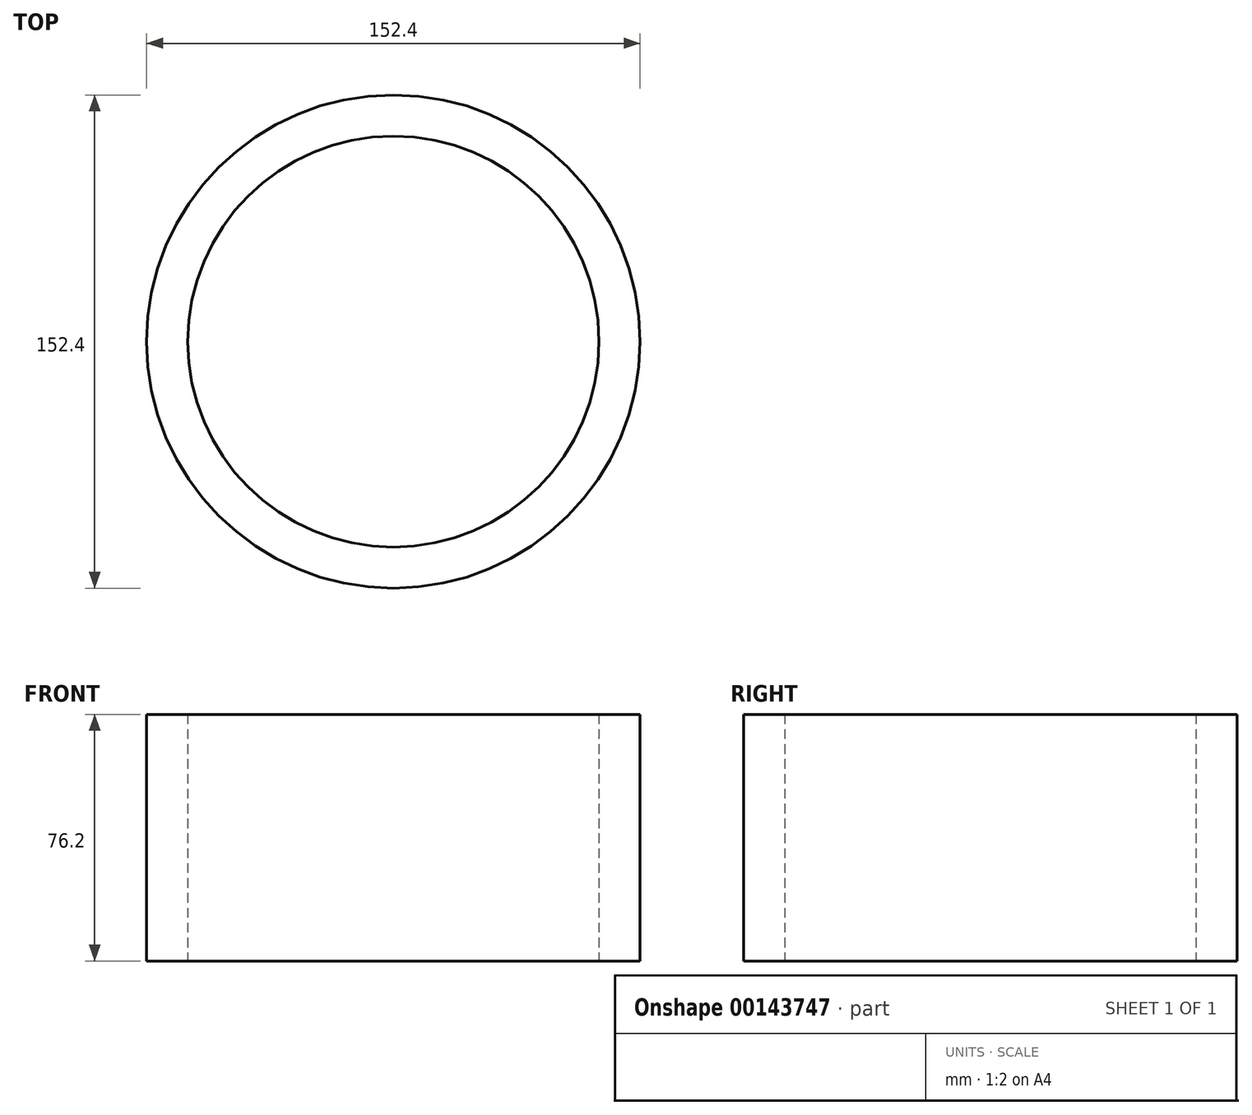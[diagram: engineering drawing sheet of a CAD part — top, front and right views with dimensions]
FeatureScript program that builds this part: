
annotation { "Feature Type Name" : "Feature", "Feature Type Description" : "" }
export const myFeature = defineFeature(function(context is Context, id is Id, definition is map)
    precondition{}
    {
        {
            var Q0;
            Q0=qCreatedBy(makeId("Top.planeOp"),FACE);
            var sketch = newSketch(context, id + "F0", { "sketchPlane" : qUnion([Q0])});
            skCircle(sketch, "E0", {"center": v(0, 0) * mm, "radius": 6.35 * mm});
            skCircle(sketch, "E1", {"center": v(0, 0) * mm, "radius": 19.05 * mm});
            skCircle(sketch, "E2", {"center": v(0, 0) * mm, "radius": 31.75 * mm});
            skCircle(sketch, "E3", {"center": v(0, 0) * mm, "radius": 63.5 * mm});
            skCircle(sketch, "E4", {"center": v(0, 0) * mm, "radius": 76.2 * mm});
            skLineSegment(sketch, "E5", {"start": v(0, 76.2) * mm, "end": v(0, -76.2) * mm, "construction": true});
            skLineSegment(sketch, "E6", {"start": v(0, -76.2) * mm, "end": v(-127, -76.2) * mm});
            skLineSegment(sketch, "E7", {"start": v(-127, -76.2) * mm, "end": v(-127, -57.15) * mm});
            skLineSegment(sketch, "E8", {"start": v(-107.95, -38.1) * mm, "end": v(-88.9, -38.1) * mm});
            skLineSegment(sketch, "E9", {"start": v(0, 76.2) * mm, "end": v(-107.95, 76.2) * mm});
            skPoint(sketch, "E9.endSnap0", {"position": v(-127, -57.15) * mm});
            skLineSegment(sketch, "E10", {"start": v(-107.95, 38.1) * mm, "end": v(-88.9, 38.1) * mm});
            skLineSegment(sketch, "E11", {"start": v(-88.9, 38.1) * mm, "end": v(-88.9, -38.1) * mm});
            skLineSegment(sketch, "E12", {"start": v(0, 76.2) * mm, "end": v(127, 76.2) * mm});
            skLineSegment(sketch, "E13", {"start": v(127, 76.2) * mm, "end": v(127, 38.1) * mm});
            skLineSegment(sketch, "E14", {"start": v(127, 38.1) * mm, "end": v(88.9, 38.1) * mm});
            skLineSegment(sketch, "E15", {"start": v(88.9, 38.1) * mm, "end": v(88.9, -38.1) * mm});
            skLineSegment(sketch, "E16", {"start": v(88.9, -38.1) * mm, "end": v(127, -38.1) * mm});
            skLineSegment(sketch, "E17", {"start": v(127, -38.1) * mm, "end": v(127, -76.2) * mm});
            skLineSegment(sketch, "E18", {"start": v(127, -76.2) * mm, "end": v(0, -76.2) * mm});
            skCircle(sketch, "E19", {"center": v(-107.95, 57.15) * mm, "radius": 9.53 * mm});
            skPoint(sketch, "E19.centerSnap0", {"position": v(-107.95, 38.1) * mm});
            skPoint(sketch, "E19.centerSnap1", {"position": v(-127, 57.15) * mm});
            skArc(sketch, "E20", {"start": v(-107.95, 76.2) * mm, "mid": v(-127, 57.15) * mm, "end": v(-107.95, 38.1) * mm});
            skPoint(sketch, "E21.orphan", {"position": v(-127, 76.2) * mm});
            skPoint(sketch, "E22.orphan", {"position": v(-127, 38.1) * mm});
            skCircle(sketch, "E23", {"center": v(-107.95, -57.15) * mm, "radius": 9.53 * mm});
            skPoint(sketch, "E23.centerSnap0", {"position": v(-107.95, -38.1) * mm});
            skCircle(sketch, "E24", {"center": v(-107.95, -57.15) * mm, "radius": 19.05 * mm});
            skPoint(sketch, "E25.orphan", {"position": v(-127, -38.1) * mm});
            skSolve(sketch);
        }
        {
            var Q0;
            Q0=qCreatedBy(makeId("Top.planeOp"),FACE);
            var sketch = newSketch(context, id + "F1", { "sketchPlane" : qUnion([Q0])});
            skCircle(sketch, "E26.0", {"center": v(0, 0) * mm, "radius": 76.2 * mm});
            skCircle(sketch, "E27.0", {"center": v(0, 0) * mm, "radius": 63.5 * mm});
            skSolve(sketch);
        }
        {
            var Q0;
            Q0 = qSketchRegion(id + "F1", true);
            extrude(context, id + "F2", {"entities" : qUnion([Q0]), "depth" : 76.2 * mm});
        }
    });
